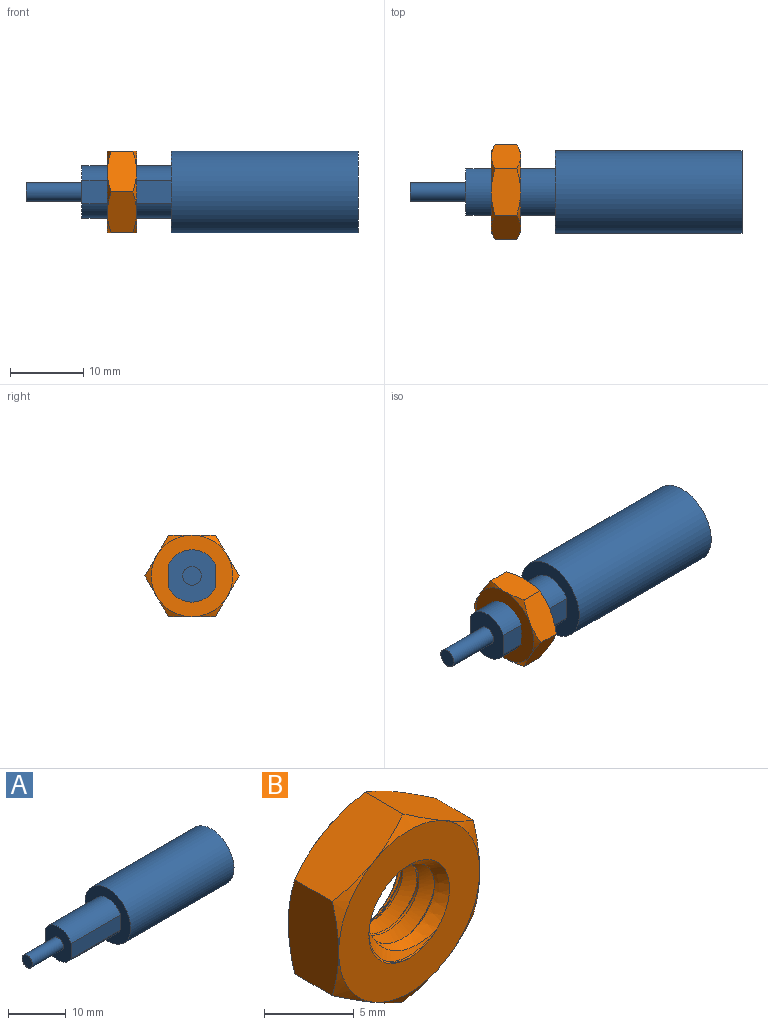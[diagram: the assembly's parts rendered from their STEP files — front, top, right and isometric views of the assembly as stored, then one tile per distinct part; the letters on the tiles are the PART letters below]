
ASSEMBLY  parts=2 mates=1
PART A: 12 faces, bbox 45.2x11.2x11.2 mm
  f0: plane 11.18x11.18mm, normal (-1,0,0), area 60mm2, adj f1,f3,f4,f5,f6
  f1: cylinder r=5.59mm len=25.4mm, axis (-1,0,0), area 891.8mm2, adj f0,f2
  f2: plane 11.18x11.18mm, normal (1,0,0), area 85.1mm2, adj f1,f8
  f3: cylinder r=3.56mm len=12.19mm, axis (1,0,0), area 95.7mm2, adj f0,f4,f6,f7
  f4: plane 12.19x3.2mm, normal (0,1,0), area 39mm2, adj f0,f3,f5,f7
  f5: cylinder r=3.56mm len=12.19mm, axis (1,0,0), area 95.7mm2, adj f0,f4,f6,f7
  f6: plane 12.19x3.2mm, normal (0,-1,0), area 39mm2, adj f0,f3,f5,f7
  f7: plane 7.11x6.35mm, normal (-1,0,0), area 33mm2, adj f3,f4,f5,f6,f10
  f8: cylinder r=2.03mm len=8.38mm, axis (1,0,0), area 107mm2, adj f2,f9
  f9: plane 4.06x4.06mm, normal (1,0,0), area 13mm2, adj f8
  f10: cylinder r=1.27mm len=7.62mm, axis (1,0,0), area 60.8mm2, adj f7,f11
  f11: plane 2.54x2.54mm, normal (-1,0,0), area 5.1mm2, adj f10
PART B: 26 faces, bbox 13.4x5.6x13.4 mm
  f0: cone r=5.56mm half-angle=60deg, axis (0,1,0), area 3mm2, adj f11,f12,f15
  f1: cone r=3.17mm half-angle=45deg, axis (0,-1,0), area 10.5mm2, adj f5,f6,f7,f15
  f2: cone r=5.56mm half-angle=60deg, axis (0,-1,0), area 3mm2, adj f8,f11,f12
  f3: cone r=3.17mm half-angle=45deg, axis (0,1,0), area 10.5mm2, adj f5,f6,f7,f8
  f4: cylinder r=3.17mm len=6.35mm, axis (0,-1,0), area 9.9mm2, adj f5,f7,f8,f15
  f5: bspline ~6.35x6.35mm, area 41.5mm2, adj f1,f3,f4,f6
  f6: cylinder r=2.35mm len=4.7mm, axis (0,-1,0), area 4.3mm2, adj f1,f3,f5,f7
  f7: bspline ~6.35x6.35mm, area 41.5mm2, adj f1,f3,f4,f6
  f8: plane 11.11x11.11mm, normal (0,1,0), area 65.3mm2, adj f2,f3,f4,f16,f17,f18,f19,f20
  f9: plane 6.08x4.5mm, normal (-0.5,0,-0.87), area 23.3mm2, adj f10,f14,f16,f20,f23,f24
  f10: plane 6.95x4.5mm, normal (-1,0,0), area 23.3mm2, adj f9,f11,f19,f20,f24,f25
  f11: plane 6.08x4.5mm, normal (-0.5,0,0.87), area 23.3mm2, adj f0,f2,f10,f12,f19,f25
  f12: plane 6.08x4.5mm, normal (0.5,0,0.87), area 23.3mm2, adj f0,f2,f11,f13,f18,f21
  f13: plane 6.95x4.5mm, normal (1,0,0), area 23.3mm2, adj f12,f14,f17,f18,f21,f22
  f14: plane 6.08x4.5mm, normal (0.5,0,-0.87), area 23.3mm2, adj f9,f13,f16,f17,f22,f23
  f15: plane 11.11x11.11mm, normal (0,-1,0), area 65.3mm2, adj f0,f1,f4,f21,f22,f23,f24,f25
  f16: cone r=5.56mm half-angle=60deg, axis (0,-1,0), area 3mm2, adj f8,f9,f14
  f17: cone r=5.56mm half-angle=60deg, axis (0,-1,0), area 3mm2, adj f8,f13,f14
  f18: cone r=5.56mm half-angle=60deg, axis (0,-1,0), area 3mm2, adj f8,f12,f13
  f19: cone r=5.56mm half-angle=60deg, axis (0,-1,0), area 3mm2, adj f8,f10,f11
  f20: cone r=5.56mm half-angle=60deg, axis (0,-1,0), area 3mm2, adj f8,f9,f10
  f21: cone r=5.56mm half-angle=60deg, axis (0,1,0), area 3mm2, adj f12,f13,f15
  f22: cone r=5.56mm half-angle=60deg, axis (0,1,0), area 3mm2, adj f13,f14,f15
  f23: cone r=5.56mm half-angle=60deg, axis (0,1,0), area 3mm2, adj f9,f14,f15
  f24: cone r=5.56mm half-angle=60deg, axis (0,1,0), area 3mm2, adj f9,f10,f15
  f25: cone r=5.56mm half-angle=60deg, axis (0,1,0), area 3mm2, adj f10,f11,f15
PLACE A at identity fixed
PLACE B rot(axis=(0.58,-0.58,0.58),120deg) t=(-6.75,0,0)mm
MATE cylindrical A.f1 <-> B.f0  axis (-1,0,0) through (0,0,0)mm
